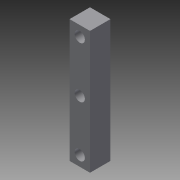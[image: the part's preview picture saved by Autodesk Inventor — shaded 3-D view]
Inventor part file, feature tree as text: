
AUTODESK INVENTOR PART (.ipt)
format: ipt  version: 2014 SP1 (Build 180222100, 222)  size: 81,920 bytes
history: native  units: in
note: dims shown in document units (in); Inventor stores cm internally (conversion verified against a paired STEP export)
features: sketch x2, extrude x1, hole x1
ambient origin geometry x8: Origin, YZ Plane, XZ Plane, XY Plane, X Axis, Y Axis, Z Axis, Center Point
bodies: Solid1 (feature_tree)
feature tree (4):
  extrude  "Extrusion1"  Depth=3.0in
  hole  "Hole1"  [1 undecoded]
  sketch  "Sketch1"  dims[d0=0.5in d1=3.0in]
  sketch  "Sketch2"  dims[d2=0.5in d3=0.0in d4=0.25in d5=0.25in d6=0.25in d7=0.75in d8=0.375in d9=0.25in d10=0.5635in d11=1.0in d12=0.8108in]
note: 1 required parameter value undecoded (feature->parameter linkage not recoverable at this tier; creation-order binding heuristic only, values carry confidence <= 0.55)
